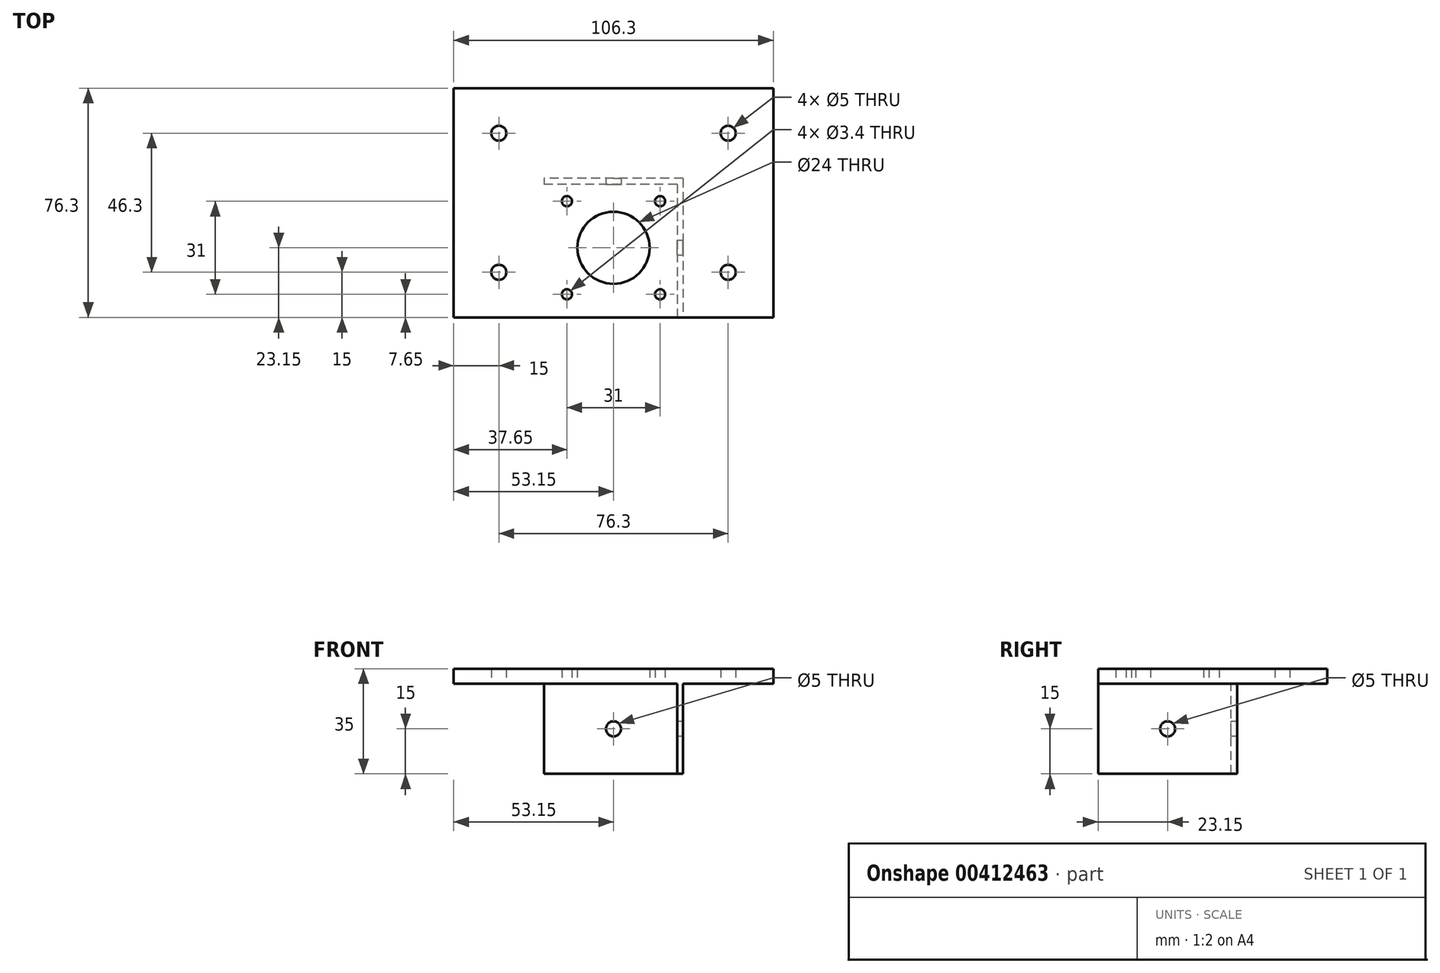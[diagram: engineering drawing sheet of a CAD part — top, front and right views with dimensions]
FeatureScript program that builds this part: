
annotation { "Feature Type Name" : "Feature", "Feature Type Description" : "" }
export const myFeature = defineFeature(function(context is Context, id is Id, definition is map)
    precondition{}
    {
        {
            var Q0;
            Q0=qCreatedBy(makeId("Top.planeOp"),FACE);
            var sketch = newSketch(context, id + "F0", { "sketchPlane" : qUnion([Q0])});
            skLineSegment(sketch, "E0.bottom", {"start": v(21.15, 21.15) * mm, "end": v(-21.15, 21.15) * mm});
            skLineSegment(sketch, "E0.top", {"start": v(21.15, -21.15) * mm, "end": v(-21.15, -21.15) * mm});
            skLineSegment(sketch, "E0.left", {"start": v(21.15, 21.15) * mm, "end": v(21.15, -21.15) * mm});
            skLineSegment(sketch, "E0.right", {"start": v(-21.15, 21.15) * mm, "end": v(-21.15, -21.15) * mm});
            skPoint(sketch, "E0.middle", {"position": v(0, 0) * mm});
            skLineSegment(sketch, "E1.bottom", {"start": v(15.5, 15.5) * mm, "end": v(-15.5, 15.5) * mm});
            skLineSegment(sketch, "E1.top", {"start": v(15.5, -15.5) * mm, "end": v(-15.5, -15.5) * mm});
            skLineSegment(sketch, "E1.left", {"start": v(15.5, 15.5) * mm, "end": v(15.5, -15.5) * mm});
            skLineSegment(sketch, "E1.right", {"start": v(-15.5, 15.5) * mm, "end": v(-15.5, -15.5) * mm});
            skCircle(sketch, "E2", {"center": v(-15.5, 15.5) * mm, "radius": 1.5 * mm});
            skCircle(sketch, "E3", {"center": v(15.5, 15.5) * mm, "radius": 1.5 * mm});
            skCircle(sketch, "E4", {"center": v(15.5, -15.5) * mm, "radius": 1.5 * mm});
            skCircle(sketch, "E5", {"center": v(-15.5, -15.5) * mm, "radius": 1.5 * mm});
            skCircle(sketch, "E6", {"center": v(0, 0) * mm, "radius": 11 * mm});
            skCircle(sketch, "E7", {"center": v(0, 0) * mm, "radius": 2.5 * mm});
            skCircle(sketch, "E8.0", {"center": v(0, 0) * mm, "radius": 12 * mm});
            skLineSegment(sketch, "E9.0", {"start": v(23.15, 23.15) * mm, "end": v(-23.15, 23.15) * mm});
            skLineSegment(sketch, "E9.1", {"start": v(23.15, 23.15) * mm, "end": v(23.15, -23.15) * mm});
            skLineSegment(sketch, "E9.2", {"start": v(23.15, -23.15) * mm, "end": v(-23.15, -23.15) * mm});
            skLineSegment(sketch, "E9.3", {"start": v(-23.15, 23.15) * mm, "end": v(-23.15, -23.15) * mm});
            skCircle(sketch, "E10.0", {"center": v(-15.5, 15.5) * mm, "radius": 1.7 * mm});
            skCircle(sketch, "E11.0", {"center": v(15.5, 15.5) * mm, "radius": 1.7 * mm});
            skCircle(sketch, "E12.0", {"center": v(15.5, -15.5) * mm, "radius": 1.7 * mm});
            skCircle(sketch, "E13.0", {"center": v(-15.5, -15.5) * mm, "radius": 1.7 * mm});
            skLineSegment(sketch, "E14.0", {"start": v(-53.15, 53.15) * mm, "end": v(-53.15, -23.15) * mm});
            skLineSegment(sketch, "E14.1", {"start": v(53.15, 53.15) * mm, "end": v(-53.15, 53.15) * mm});
            skLineSegment(sketch, "E14.2", {"start": v(53.15, 53.15) * mm, "end": v(53.15, -23.15) * mm});
            skLineSegment(sketch, "E15", {"start": v(-53.15, -23.15) * mm, "end": v(-23.15, -23.15) * mm});
            skLineSegment(sketch, "E16", {"start": v(23.15, -23.15) * mm, "end": v(53.15, -23.15) * mm});
            skCircle(sketch, "E17", {"center": v(-38.15, 38.15) * mm, "radius": 2.5 * mm});
            skCircle(sketch, "E18", {"center": v(38.15, 38.15) * mm, "radius": 2.5 * mm});
            skCircle(sketch, "E19", {"center": v(-38.15, -8.15) * mm, "radius": 2.5 * mm});
            skCircle(sketch, "E20", {"center": v(38.15, -8.15) * mm, "radius": 2.5 * mm});
            skLineSegment(sketch, "E21", {"start": v(-21.15, 21.15) * mm, "end": v(-23.15, 21.15) * mm});
            skLineSegment(sketch, "E22", {"start": v(21.15, 21.15) * mm, "end": v(23.15, 21.15) * mm});
            skLineSegment(sketch, "E23", {"start": v(21.15, -21.15) * mm, "end": v(21.15, -23.15) * mm});
            skLineSegment(sketch, "E24", {"start": v(-21.15, -21.15) * mm, "end": v(-21.15, -23.15) * mm});
            skSolve(sketch);
        }
        {
            var Q0;
            Q0=makeQuery(id+"F0.imprint","IMPRINT",FACE,{"disambiguationData":[TD([[makeQuery(id+"F0.imprint","IMPRINT",EDGE,{"derivedFrom":sQuery(id+"F0.wireOp",EDGE,"E0.bottom")}),-1.0]])]});
            var Q1;
            Q1=makeQuery(id+"F0.imprint","IMPRINT",FACE,{"disambiguationData":[TD([[makeQuery(id+"F0.imprint","IMPRINT",EDGE,{"derivedFrom":sQuery(id+"F0.wireOp",EDGE,"E0.bottom")}),1.0]])]});
            var Q2;
            Q2=makeQuery(id+"F0.imprint","IMPRINT",FACE,{"disambiguationData":[TD([[makeQuery(id+"F0.imprint","IMPRINT",EDGE,{"derivedFrom":sQuery(id+"F0.wireOp",EDGE,"E8.0")}),-1.0]])]});
            var Q3;
            Q3=makeQuery(id+"F0.imprint","IMPRINT",FACE,{"disambiguationData":[TD([[makeQuery(id+"F0.imprint","IMPRINT",EDGE,{"derivedFrom":sQuery(id+"F0.wireOp",EDGE,"E9.0")}),-1.0]])]});
            var Q4;
            Q4=makeQuery(id+"F0.imprint","IMPRINT",FACE,{"disambiguationData":[TD([[makeQuery(id+"F0.imprint","IMPRINT",EDGE,{"derivedFrom":sQuery(id+"F0.wireOp",EDGE,"E0.right")}),-1.0]])]});
            var Q5;
            Q5=makeQuery(id+"F0.imprint","IMPRINT",FACE,{"disambiguationData":[TD([[makeQuery(id+"F0.imprint","IMPRINT",EDGE,{"derivedFrom":sQuery(id+"F0.wireOp",EDGE,"E0.left")}),1.0]])]});
            var Q6;
            Q6=makeQuery(id+"F0.imprint","IMPRINT",FACE,{"disambiguationData":[TD([[makeQuery(id+"F0.imprint","IMPRINT",EDGE,{"derivedFrom":sQuery(id+"F0.wireOp",EDGE,"E0.top")}),1.0]])]});
            extrude(context, id + "F1", {"entities" : qUnion([Q0, Q1, Q2, Q3, Q4, Q5, Q6]), "depth" : 5 * mm});
        }
        {
            var Q0;
            Q0=makeQuery(id+"F0.imprint","IMPRINT",FACE,{"disambiguationData":[TD([[makeQuery(id+"F0.imprint","IMPRINT",EDGE,{"derivedFrom":sQuery(id+"F0.wireOp",EDGE,"E0.bottom")}),-1.0]])]});
            var Q1;
            Q1=makeQuery(id+"F0.imprint","IMPRINT",FACE,{"disambiguationData":[TD([[makeQuery(id+"F0.imprint","IMPRINT",EDGE,{"derivedFrom":sQuery(id+"F0.wireOp",EDGE,"E0.left")}),1.0]])]});
            extrude(context, id + "F2", {"entities" : qUnion([Q0, Q1]), "operationType" : NewBodyOperationType.ADD, "oppositeDirection" : true, "depth" : 30 * mm});
        }
        {
            var Q0;
            Q0=makeQuery(id+"F2.opExtrude","SWEPT_FACE",FACE,{"disambiguationData":[OSD([sQuery(id+"F0.wireOp",EDGE,"E0.bottom"),sQuery(id+"F0.wireOp",EDGE,"E21")])]});
            var sketch = newSketch(context, id + "F3", { "sketchPlane" : qUnion([Q0])});
            skPoint(sketch, "E25", {"position": v(0, -15) * mm});
            skSolve(sketch);
        }
        {
            var Q0;
            Q0=makeQuery(id+"F2.opExtrude","SWEPT_FACE",FACE,{"disambiguationData":[OSD([sQuery(id+"F0.wireOp",EDGE,"E0.left"),sQuery(id+"F0.wireOp",EDGE,"E23")])]});
            var sketch = newSketch(context, id + "F4", { "sketchPlane" : qUnion([Q0])});
            skPoint(sketch, "E26", {"position": v(0, -15) * mm});
            skSolve(sketch);
        }
        {
            var Q0;
            Q0=sQuery(id+"F3.wireOp",VERTEX,"E25");
            var Q1;
            Q1=sQuery(id+"F4.wireOp",VERTEX,"E26");
            var Q2;
            Q2=makeQuery(id+"F1.opExtrude","SWEPT_BODY",BODY,{"disambiguationData":[OSD([sQuery(id+"F0.wireOp",EDGE,"E8.0"),sQuery(id+"F0.wireOp",EDGE,"E9.2"),sQuery(id+"F0.wireOp",EDGE,"E10.0"),sQuery(id+"F0.wireOp",EDGE,"E11.0"),sQuery(id+"F0.wireOp",EDGE,"E12.0"),sQuery(id+"F0.wireOp",EDGE,"E13.0"),sQuery(id+"F0.wireOp",EDGE,"E14.0"),sQuery(id+"F0.wireOp",EDGE,"E14.1"),sQuery(id+"F0.wireOp",EDGE,"E14.2"),sQuery(id+"F0.wireOp",EDGE,"E15"),sQuery(id+"F0.wireOp",EDGE,"E16"),sQuery(id+"F0.wireOp",EDGE,"E17"),sQuery(id+"F0.wireOp",EDGE,"E18"),sQuery(id+"F0.wireOp",EDGE,"E19"),sQuery(id+"F0.wireOp",EDGE,"E20")])]});
            hole(context, id + "F5", {"style" : HoleStyle.SIMPLE, "endStyle" : HoleEndStyle.BLIND, "holeDiameter" : 5 * mm, "holeDepth" : 12.7 * mm, "isTappedThrough" : true, "tappedDepth" : 12 * mm, "tapClearance" : 3, "locations" : qUnion([Q0, Q1]), "scope" : qUnion([Q2])});
        }
    });
